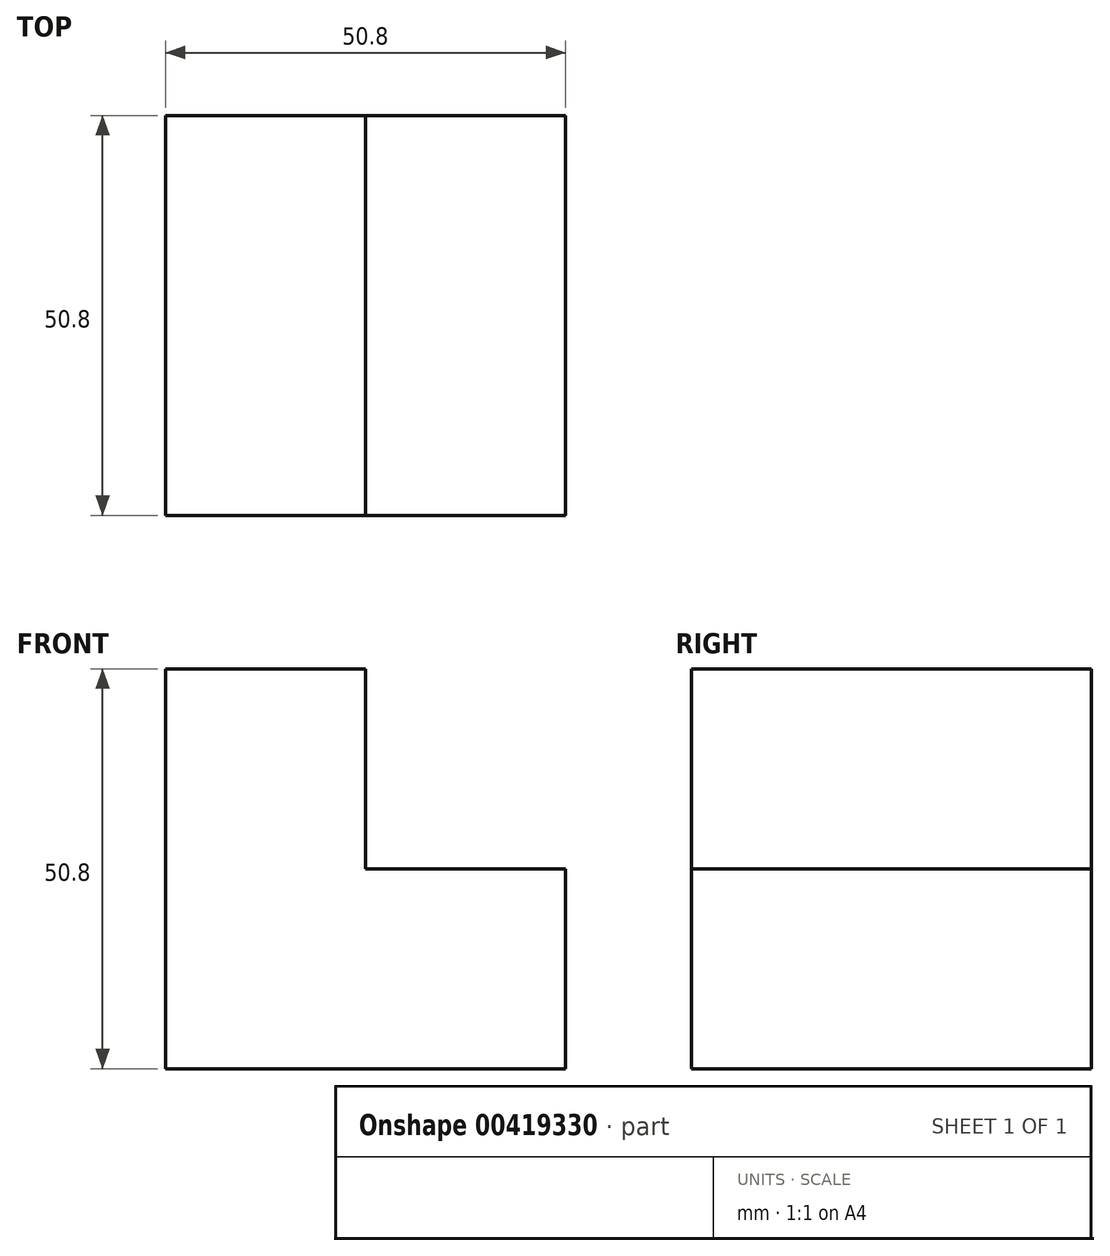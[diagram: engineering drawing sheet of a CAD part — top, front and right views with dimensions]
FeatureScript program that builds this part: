
annotation { "Feature Type Name" : "Feature", "Feature Type Description" : "" }
export const myFeature = defineFeature(function(context is Context, id is Id, definition is map)
    precondition{}
    {
        {
            var Q0;
            Q0=qCreatedBy(makeId("Front.planeOp"),FACE);
            var sketch = newSketch(context, id + "F0", { "sketchPlane" : qUnion([Q0])});
            skLineSegment(sketch, "E0", {"start": v(0, 0) * mm, "end": v(-50.8, 0) * mm});
            skLineSegment(sketch, "E1", {"start": v(-50.8, 0) * mm, "end": v(-50.8, 50.8) * mm});
            skLineSegment(sketch, "E2", {"start": v(-50.8, 50.8) * mm, "end": v(-25.4, 50.8) * mm});
            skLineSegment(sketch, "E3", {"start": v(-25.4, 50.8) * mm, "end": v(-25.4, 25.4) * mm});
            skLineSegment(sketch, "E4", {"start": v(-25.4, 25.4) * mm, "end": v(0, 25.4) * mm});
            skLineSegment(sketch, "E5", {"start": v(0, 25.4) * mm, "end": v(0, 0) * mm});
            skSolve(sketch);
        }
        {
            var Q0;
            Q0=makeQuery(id+"F0.imprint","IMPRINT",FACE,{"disambiguationData":[TD([[makeQuery(id+"F0.imprint","IMPRINT",EDGE,{"derivedFrom":sQuery(id+"F0.wireOp",EDGE,"E0")}),-1.0]])]});
            extrude(context, id + "F1", {"entities" : qUnion([Q0]), "oppositeDirection" : true, "depth" : 50.8 * mm});
        }
    });
